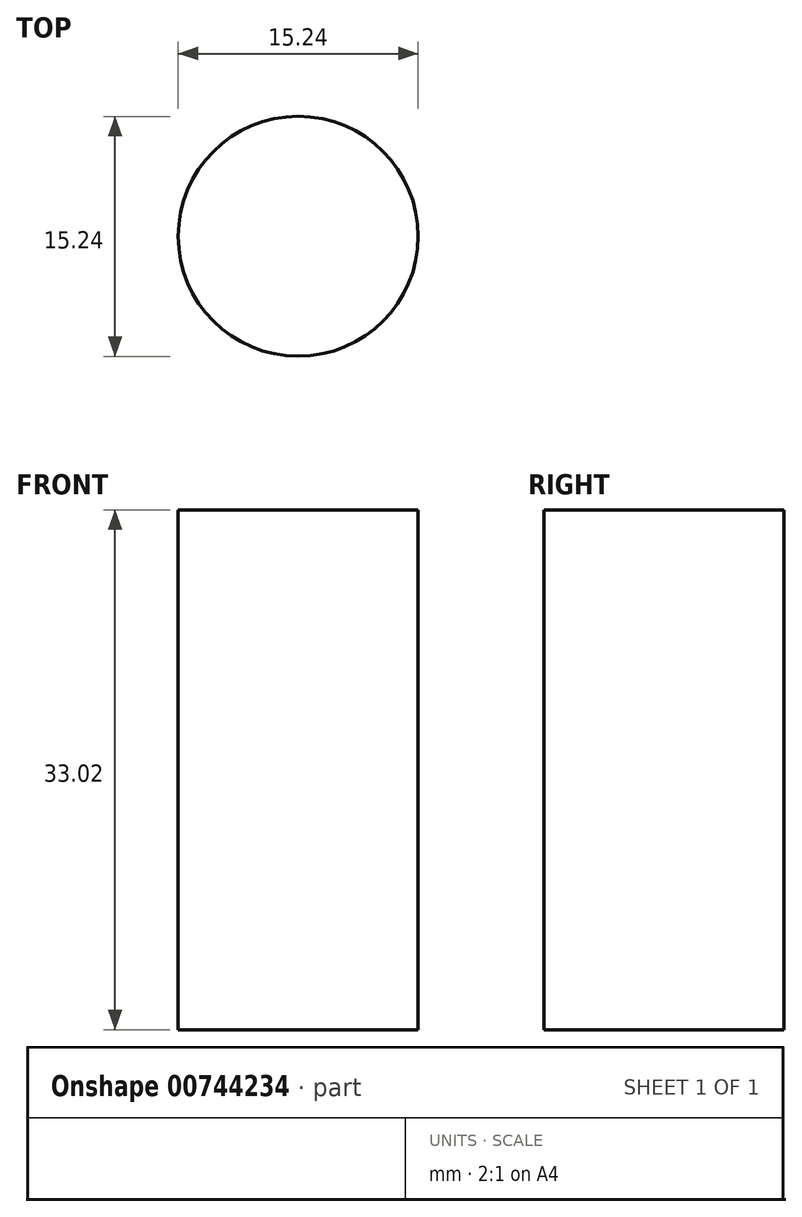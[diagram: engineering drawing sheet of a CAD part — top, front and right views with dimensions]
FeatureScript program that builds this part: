
annotation { "Feature Type Name" : "Feature", "Feature Type Description" : "" }
export const myFeature = defineFeature(function(context is Context, id is Id, definition is map)
    precondition{}
    {
        {
            var Q0;
            Q0=qCreatedBy(makeId("Top.planeOp"),FACE);
            var sketch = newSketch(context, id + "F0", { "sketchPlane" : qUnion([Q0])});
            skCircle(sketch, "E0", {"center": v(-29.24, 29.1) * mm, "radius": 7.62 * mm});
            skSolve(sketch);
        }
        {
            var Q0;
            Q0=makeQuery(id+"F0.imprint","IMPRINT",FACE,{"disambiguationData":[TD([[makeQuery(id+"F0.imprint","IMPRINT",EDGE,{"derivedFrom":sQuery(id+"F0.wireOp",EDGE,"E0")}),1.0]])]});
            extrude(context, id + "F1", {"entities" : qUnion([Q0]), "depth" : 33.02 * mm, "offsetDistance" : 25.4 * mm});
        }
    });
